# Revit family: Kiosk
name_source: partatom
category: Security Devices
units: mm (PartAtom-declared; Revit-internal decimal feet)

## family parameters
Always vertical = No
Cut with Voids When Loaded = No
Maintain Annotation Orientation = No
OmniClass Number = 23.85.50.17
OmniClass Title = Communication and Data Processing Equipment
Part Type = Normal
Room Calculation Point = No
Round Connector Dimension = Use Diameter
Shared = No
Work Plane-Based = Yes

## types (3) — shared parameters
Default Elevation = 0' - 0"
Desk Mount Length = 1' - 0"
Manufacturer = Athena Security
URL = https://www.athena-security.com

## per-type parameters (varying)
| type | Mounting Height |
| Default | 3' - 6" |
| Wall Mount | 3' - 6" |
| Desk Mount | 3' - 0" |

type visibility flags (boolean, named after types; folded from table):
- Default: Yes: Desk Mount
- Wall Mount: Yes: Wall Mount
- Desk Mount: Yes: Desk Mount

## geometry (parser evidence)
native form markers: Sweep x11
no freeform markers — native parametric forms only
